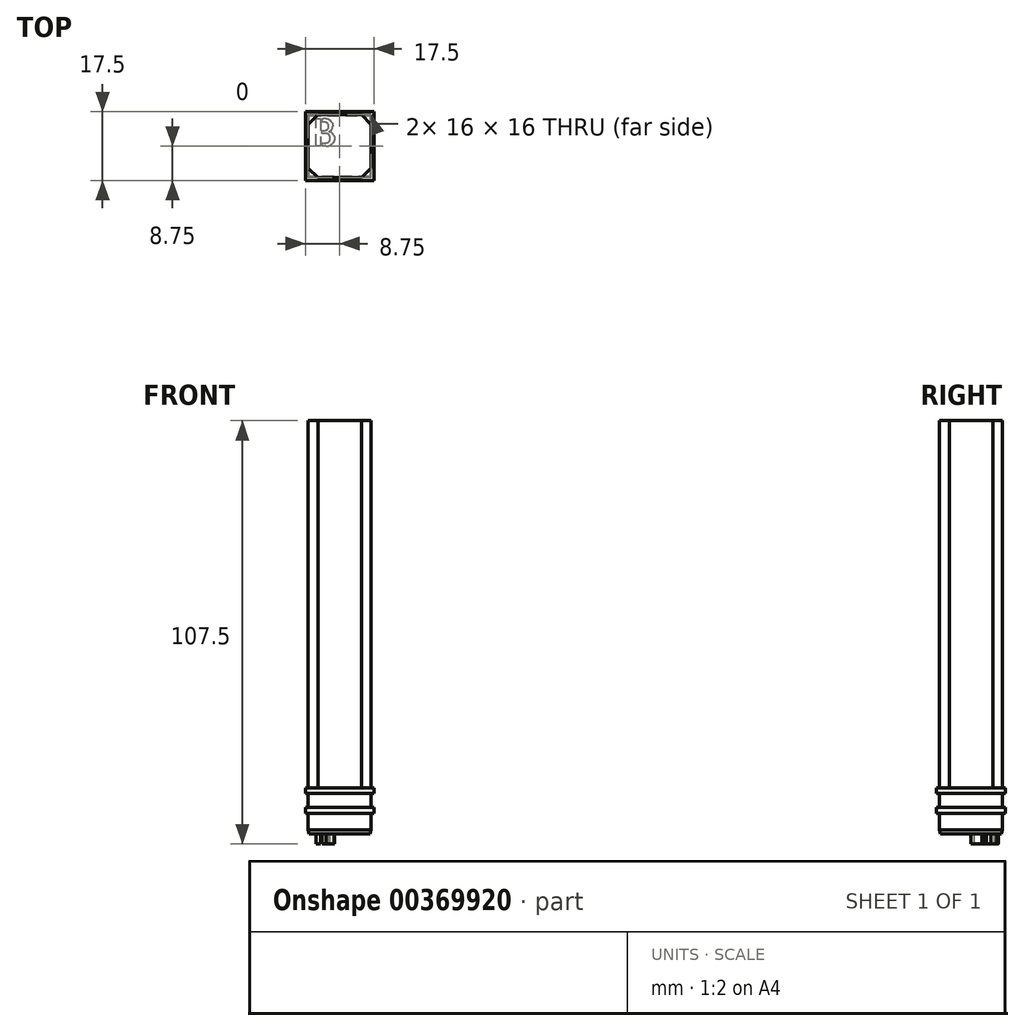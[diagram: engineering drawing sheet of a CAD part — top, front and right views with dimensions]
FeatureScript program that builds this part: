
annotation { "Feature Type Name" : "Feature", "Feature Type Description" : "" }
export const myFeature = defineFeature(function(context is Context, id is Id, definition is map)
    precondition{}
    {
        {
            var Q0;
            Q0=qCreatedBy(makeId("Top.planeOp"),FACE);
            var sketch = newSketch(context, id + "F0", { "sketchPlane" : qUnion([Q0])});
            skLineSegment(sketch, "E0.bottom", {"start": v(7.5, -7.5) * mm, "end": v(-7.5, -7.5) * mm, "construction": true});
            skLineSegment(sketch, "E0.top", {"start": v(7.5, 7.5) * mm, "end": v(-7.5, 7.5) * mm, "construction": true});
            skLineSegment(sketch, "E0.left", {"start": v(7.5, -7.5) * mm, "end": v(7.5, 7.5) * mm, "construction": true});
            skLineSegment(sketch, "E0.right", {"start": v(-7.5, -7.5) * mm, "end": v(-7.5, 7.5) * mm, "construction": true});
            skPoint(sketch, "E0.middle", {"position": v(0, 0) * mm});
            skLineSegment(sketch, "E1.0", {"start": v(8, -8) * mm, "end": v(8, 8) * mm});
            skLineSegment(sketch, "E1.1", {"start": v(8, -8) * mm, "end": v(-8, -8) * mm});
            skLineSegment(sketch, "E1.2", {"start": v(-8, -8) * mm, "end": v(-8, 8) * mm});
            skLineSegment(sketch, "E1.3", {"start": v(8, 8) * mm, "end": v(-8, 8) * mm});
            skLineSegment(sketch, "E2.0", {"start": v(7, 7) * mm, "end": v(-7, 7) * mm});
            skLineSegment(sketch, "E2.1", {"start": v(7, -7) * mm, "end": v(7, 7) * mm});
            skLineSegment(sketch, "E2.2", {"start": v(7, -7) * mm, "end": v(-7, -7) * mm});
            skLineSegment(sketch, "E2.3", {"start": v(-7, -7) * mm, "end": v(-7, 7) * mm});
            skLineSegment(sketch, "E3", {"start": v(0, 7) * mm, "end": v(0, -7) * mm, "construction": true});
            skLineSegment(sketch, "E4", {"start": v(-7, 0) * mm, "end": v(7, 0) * mm, "construction": true});
            skSolve(sketch);
        }
        {
            var Q0;
            Q0=qCreatedBy(makeId("Top.planeOp"),FACE);
            var sketch = newSketch(context, id + "F1", { "sketchPlane" : qUnion([Q0])});
            skPoint(sketch, "E5.0", {"position": v(0, 7) * mm});
            skPoint(sketch, "E6.0", {"position": v(0, 0) * mm});
            skPoint(sketch, "E7.0", {"position": v(7, 0) * mm});
            skPoint(sketch, "E8.0", {"position": v(7, 7) * mm});
            skLineSegment(sketch, "E9", {"start": v(0, 7) * mm, "end": v(0, 0) * mm, "construction": true});
            skLineSegment(sketch, "E10", {"start": v(7, 0) * mm, "end": v(0, 0) * mm, "construction": true});
            skLineSegment(sketch, "E11", {"start": v(7, 7) * mm, "end": v(7, 0) * mm, "construction": true});
            skLineSegment(sketch, "E12", {"start": v(7, 7) * mm, "end": v(0, 7) * mm, "construction": true});
            skText(sketch, "E13", { "text": "Default text", "fontName": "OpenSans-Regular.ttf"});
            skText(sketch, "E14", { "text": "Default text", "fontName": "RobotoSlab-Regular.ttf"});
            skText(sketch, "E15", { "text": "Default text", "fontName": "Tinos-Regular.ttf"});
            skText(sketch, "E16", { "text": "Default text", "fontName": "NotoSerif-Regular.ttf"});
            skText(sketch, "E17", { "text": "Default text", "fontName": "NotoSansCJKkr-Regular.otf"});
            skText(sketch, "E18", { "text": "Default text", "fontName": "NotoSansCJKjp-Regular.otf"});
            skText(sketch, "E19", { "text": "Default text", "fontName": "NotoSansCJKtc-Regular.otf"});
            skText(sketch, "E20", { "text": "Default text", "fontName": "NotoSansCJKsc-Regular.otf"});
            skText(sketch, "E21", { "text": "Default text", "fontName": "NotoSans-Regular.ttf"});
            skText(sketch, "E22", { "text": "Default text", "fontName": "DroidSansMono.ttf"});
            skText(sketch, "E23", { "text": "Default text", "fontName": "Arimo-Regular.ttf"});
            skText(sketch, "E24", { "text": "Default text", "fontName": "AllertaStencil-Regular.ttf"});
            skPoint(sketch, "E25.0", {"position": v(-7, 0) * mm});
            skPoint(sketch, "E26.0", {"position": v(-7, 7) * mm});
            skLineSegment(sketch, "E27", {"start": v(-5.99, 6.3) * mm, "end": v(-5.99, 0.6) * mm});
            skLineSegment(sketch, "E28", {"start": v(-5.99, 0.6) * mm, "end": v(-4.25, 0.6) * mm});
            skLineSegment(sketch, "E29", {"start": v(-5.99, 6.3) * mm, "end": v(-4.25, 6.3) * mm});
            skArc(sketch, "E30", {"start": v(-2.96, 3.45) * mm, "mid": v(-2.68, 5.3) * mm, "end": v(-4.25, 6.3) * mm});
            skPoint(sketch, "E30.startSnap0", {"position": v(-5.99, 3.45) * mm});
            skArc(sketch, "E31", {"start": v(-4.25, 0.6) * mm, "mid": v(-2.68, 1.6) * mm, "end": v(-2.96, 3.45) * mm});
            skLineSegment(sketch, "E32.0", {"start": v(-4.99, 6.3) * mm, "end": v(-4.99, 0.6) * mm, "construction": true});
            skLineSegment(sketch, "E33.0", {"start": v(-5.99, 1.6) * mm, "end": v(-4.25, 1.6) * mm, "construction": true});
            skLineSegment(sketch, "E34.0", {"start": v(-5.99, 5.3) * mm, "end": v(-4.25, 5.3) * mm, "construction": true});
            skLineSegment(sketch, "E35", {"start": v(-5.99, 3.45) * mm, "end": v(-4.25, 3.45) * mm, "construction": true});
            skLineSegment(sketch, "E36.0", {"start": v(-5.99, 2.95) * mm, "end": v(-4.25, 2.95) * mm, "construction": true});
            skLineSegment(sketch, "E37.0", {"start": v(-5.99, 3.95) * mm, "end": v(-4.25, 3.95) * mm, "construction": true});
            skArc(sketch, "E38", {"start": v(-4.25, 3.95) * mm, "mid": v(-3.57, 4.63) * mm, "end": v(-4.25, 5.3) * mm});
            skArc(sketch, "E39", {"start": v(-4.25, 1.6) * mm, "mid": v(-3.57, 2.27) * mm, "end": v(-4.25, 2.95) * mm});
            skLineSegment(sketch, "E40", {"start": v(-4.25, 2.95) * mm, "end": v(-4.99, 2.95) * mm});
            skLineSegment(sketch, "E41", {"start": v(-4.99, 2.95) * mm, "end": v(-4.99, 1.6) * mm});
            skLineSegment(sketch, "E42", {"start": v(-4.99, 1.6) * mm, "end": v(-4.25, 1.6) * mm});
            skLineSegment(sketch, "E43", {"start": v(-4.25, 3.95) * mm, "end": v(-4.99, 3.95) * mm});
            skLineSegment(sketch, "E44", {"start": v(-4.99, 3.95) * mm, "end": v(-4.99, 5.3) * mm});
            skLineSegment(sketch, "E45", {"start": v(-4.99, 5.3) * mm, "end": v(-4.25, 5.3) * mm});
            const initialGuessF1  = {"E13": [0.01056, 0.00091, 1, 0, 0.0074], "E14": [0.01974, -0.0134, 1, 0, 0.00915], "E15": [0.01862, -0.02922, 1, 0, 0.01054], "E16": [0.01728, -0.04803, 1, 0, 0.015], "E17": [0.0163, -0.07044, 1, 0, 0.01509], "E18": [0.01548, -0.0952, 1, 0, 0.01868], "E19": [0.01736, -0.1088, 1, 0, 0.00829], "E20": [0.0176, -0.12018, 1, 0, 0.00556], "E21": [0.0185, -0.12816, 1, 0, 0.00542], "E22": [0.01813, -0.13854, 1, 0, 0.0054], "E23": [0.01918, -0.14712, 1, 0, 0.00545], "E24": [0.0191, -0.1535, 1, 0, 0.00425]};
            skSetInitialGuess(sketch, initialGuessF1);
            skSolve(sketch);
        }
        {
            var Q0;
            Q0=makeQuery(id+"F1.imprint","IMPRINT",FACE,{"disambiguationData":[TD([[makeQuery(id+"F1.imprint","IMPRINT",EDGE,{"derivedFrom":sQuery(id+"F1.wireOp",EDGE,"E27")}),1.0]])]});
            var Q1;
            Q1=makeQuery(id+"F0.imprint","IMPRINT",FACE,{"disambiguationData":[TD([[makeQuery(id+"F0.imprint","IMPRINT",EDGE,{"derivedFrom":sQuery(id+"F0.wireOp",EDGE,"E1.0")}),1.0]])]});
            extrude(context, id + "F2", {"entities" : qUnion([Q0, Q1]), "depth" : 5 * mm, "offsetDistance" : 25 * mm});
        }
        {
            var Q0;
            Q0=makeQuery(id+"F2.opExtrude","CAP_EDGE",EDGE,{"disambiguationData":[OSD([sQuery(id+"F0.wireOp",EDGE,"E1.0")])],"isStart":true});
            var Q1;
            Q1=makeQuery(id+"F2.opExtrude","CAP_EDGE",EDGE,{"disambiguationData":[OSD([sQuery(id+"F0.wireOp",EDGE,"E1.1")])],"isStart":true});
            var Q2;
            Q2=makeQuery(id+"F2.opExtrude","CAP_EDGE",EDGE,{"disambiguationData":[OSD([sQuery(id+"F0.wireOp",EDGE,"E1.2")])],"isStart":true});
            var Q3;
            Q3=makeQuery(id+"F2.opExtrude","CAP_EDGE",EDGE,{"disambiguationData":[OSD([sQuery(id+"F0.wireOp",EDGE,"E1.3")])],"isStart":true});
            var Q4;
            Q4=makeQuery(id+"F2.opExtrude","CAP_EDGE",EDGE,{"disambiguationData":[OSD([sQuery(id+"F0.wireOp",EDGE,"E2.1")])],"isStart":true});
            var Q5;
            Q5=makeQuery(id+"F2.opExtrude","CAP_EDGE",EDGE,{"disambiguationData":[OSD([sQuery(id+"F0.wireOp",EDGE,"E2.0")])],"isStart":true});
            var Q6;
            Q6=makeQuery(id+"F2.opExtrude","CAP_EDGE",EDGE,{"disambiguationData":[OSD([sQuery(id+"F0.wireOp",EDGE,"E2.3")])],"isStart":true});
            var Q7;
            Q7=makeQuery(id+"F2.opExtrude","CAP_EDGE",EDGE,{"disambiguationData":[OSD([sQuery(id+"F0.wireOp",EDGE,"E2.2")])],"isStart":true});
            chamfer(context, id + "F3", {"entities" : qUnion([Q0, Q1, Q2, Q3, Q4, Q5, Q6, Q7]), "chamferType" : ChamferType.TWO_OFFSETS, "width1" : 1 * mm, "oppositeDirection" : false, "width2" : .25 * mm, "tangentPropagation" : true});
        }
        {
            var Q0;
            Q0=makeQuery(id+"F2.opExtrude","CAP_EDGE",EDGE,{"disambiguationData":[OSD([sQuery(id+"F1.wireOp",EDGE,"E27")])],"isStart":true});
            var Q1;
            Q1=makeQuery(id+"F2.opExtrude","CAP_EDGE",EDGE,{"disambiguationData":[OSD([sQuery(id+"F1.wireOp",EDGE,"E28")])],"isStart":true});
            var Q2;
            Q2=makeQuery(id+"F2.opExtrude","CAP_EDGE",EDGE,{"disambiguationData":[OSD([sQuery(id+"F1.wireOp",EDGE,"E31")])],"isStart":true});
            var Q3;
            Q3=makeQuery(id+"F2.opExtrude","CAP_EDGE",EDGE,{"disambiguationData":[OSD([sQuery(id+"F1.wireOp",EDGE,"E30")])],"isStart":true});
            var Q4;
            Q4=makeQuery(id+"F2.opExtrude","CAP_EDGE",EDGE,{"disambiguationData":[OSD([sQuery(id+"F1.wireOp",EDGE,"E29")])],"isStart":true});
            var Q5;
            Q5=makeQuery(id+"F2.opExtrude","CAP_EDGE",EDGE,{"disambiguationData":[OSD([sQuery(id+"F1.wireOp",EDGE,"E40")])],"isStart":true});
            var Q6;
            Q6=makeQuery(id+"F2.opExtrude","CAP_EDGE",EDGE,{"disambiguationData":[OSD([sQuery(id+"F1.wireOp",EDGE,"E41")])],"isStart":true});
            var Q7;
            Q7=makeQuery(id+"F2.opExtrude","CAP_EDGE",EDGE,{"disambiguationData":[OSD([sQuery(id+"F1.wireOp",EDGE,"E44")])],"isStart":true});
            var Q8;
            Q8=makeQuery(id+"F2.opExtrude","CAP_EDGE",EDGE,{"disambiguationData":[OSD([sQuery(id+"F1.wireOp",EDGE,"E45")])],"isStart":true});
            chamfer(context, id + "F4", {"entities" : qUnion([Q0, Q1, Q2, Q3, Q4, Q5, Q6, Q7, Q8]), "chamferType" : ChamferType.TWO_OFFSETS, "width1" : 1 * mm, "oppositeDirection" : false, "width2" : .25 * mm, "tangentPropagation" : true});
        }
        {
            var Q0;
            Q0=makeQuery(id+"F2.opExtrude","CAP_FACE",FACE,{"disambiguationData":[OSD([sQuery(id+"F0.wireOp",EDGE,"E1.0"),sQuery(id+"F0.wireOp",EDGE,"E1.1"),sQuery(id+"F0.wireOp",EDGE,"E1.2"),sQuery(id+"F0.wireOp",EDGE,"E1.3"),sQuery(id+"F0.wireOp",EDGE,"E2.0"),sQuery(id+"F0.wireOp",EDGE,"E2.1"),sQuery(id+"F0.wireOp",EDGE,"E2.2"),sQuery(id+"F0.wireOp",EDGE,"E2.3")])],"isStart":false});
            var sketch = newSketch(context, id + "F5", { "sketchPlane" : qUnion([Q0])});
            skPoint(sketch, "E46.0", {"position": v(-8, 8) * mm});
            skPoint(sketch, "E47.0", {"position": v(7, 7) * mm});
            skPoint(sketch, "E48.0", {"position": v(-8, -8) * mm});
            skPoint(sketch, "E49.0", {"position": v(8, -8) * mm});
            skLineSegment(sketch, "E50.bottom", {"start": v(-8, 8) * mm, "end": v(8, 8) * mm});
            skLineSegment(sketch, "E50.top", {"start": v(-8, -8) * mm, "end": v(8, -8) * mm});
            skLineSegment(sketch, "E50.left", {"start": v(-8, 8) * mm, "end": v(-8, -8) * mm});
            skLineSegment(sketch, "E50.right", {"start": v(8, 8) * mm, "end": v(8, -8) * mm});
            skSolve(sketch);
        }
        {
            var Q0;
            Q0 = qSketchRegion(id + "F5", true);
            extrude(context, id + "F6", {"entities" : qUnion([Q0]), "depth" : 25 * mm, "offsetDistance" : 25 * mm, "hasSecondDirection" : true, "secondDirectionOppositeDirection" : true, "secondDirectionDepth" : 4 * mm});
        }
        {
            var Q0;
            Q0=makeQuery(id+"F6.opExtrude","CAP_FACE",FACE,{"disambiguationData":[OSD([sQuery(id+"F5.wireOp",EDGE,"E50.bottom"),sQuery(id+"F5.wireOp",EDGE,"E50.top"),sQuery(id+"F5.wireOp",EDGE,"E50.left"),sQuery(id+"F5.wireOp",EDGE,"E50.right")])],"isStart":false});
            extrude(context, id + "F7", {"entities" : qUnion([Q0]), "operationType" : NewBodyOperationType.ADD, "depth" : 25 * mm, "offsetDistance" : 25 * mm});
        }
        {
            var Q0;
            Q0=makeQuery(id+"F6.boolean.opBoolean","SPLIT",FACE,{"disambiguationData":[TD([makeQuery(id+"F3.opChamfer","BLEND_FACE",FACE,{"disambiguationData":[OSD([sQuery(id+"F0.wireOp",EDGE,"E2.0")])]})])],"derivedFrom":makeQuery(id+"F6.opExtrude","CAP_FACE",FACE,{"disambiguationData":[OSD([sQuery(id+"F5.wireOp",EDGE,"E50.bottom"),sQuery(id+"F5.wireOp",EDGE,"E50.top"),sQuery(id+"F5.wireOp",EDGE,"E50.left"),sQuery(id+"F5.wireOp",EDGE,"E50.right")])],"isStart":true})});
            cPlane(context, id + "F8", {"entities" : qUnion([Q0]), "cplaneType" : CPlaneType.OFFSET, "offset" : 5 * mm, "oppositeDirection" : true, "width" : 150 * mm, "height" : 150 * mm});
        }
        {
            var Q0;
            Q0=qCreatedBy(id+"F8.planeOp",FACE);
            cPlane(context, id + "F9", {"entities" : qUnion([Q0]), "cplaneType" : CPlaneType.OFFSET, "offset" : 5 * mm, "oppositeDirection" : true, "width" : 150 * mm, "height" : 150 * mm});
        }
        {
            var Q0;
            Q0=qCreatedBy(id+"F8.planeOp",FACE);
            var sketch = newSketch(context, id + "F10", { "sketchPlane" : qUnion([Q0])});
            skLineSegment(sketch, "E51.0.1", {"start": v(-8, -8) * mm, "end": v(-8, 8) * mm});
            skLineSegment(sketch, "E51.0.3", {"start": v(-8, 8) * mm, "end": v(-8, -8) * mm});
            skLineSegment(sketch, "E52.0.1", {"start": v(8, -8) * mm, "end": v(-8, -8) * mm});
            skLineSegment(sketch, "E52.0.3", {"start": v(-8, -8) * mm, "end": v(8, -8) * mm});
            skLineSegment(sketch, "E53.0.1", {"start": v(8, 8) * mm, "end": v(8, -8) * mm});
            skLineSegment(sketch, "E53.0.3", {"start": v(8, -8) * mm, "end": v(8, 8) * mm});
            skLineSegment(sketch, "E54.0.1", {"start": v(-8, 8) * mm, "end": v(8, 8) * mm});
            skLineSegment(sketch, "E54.0.3", {"start": v(8, 8) * mm, "end": v(-8, 8) * mm});
            skSolve(sketch);
        }
        {
            var Q0;
            Q0=qCreatedBy(id+"F9.planeOp",FACE);
            var sketch = newSketch(context, id + "F11", { "sketchPlane" : qUnion([Q0])});
            skLineSegment(sketch, "E55.0.1", {"start": v(-8, 8) * mm, "end": v(8, 8) * mm});
            skLineSegment(sketch, "E55.0.3", {"start": v(8, 8) * mm, "end": v(-8, 8) * mm});
            skLineSegment(sketch, "E56.0.1", {"start": v(8, 8) * mm, "end": v(8, -8) * mm});
            skLineSegment(sketch, "E56.0.3", {"start": v(8, -8) * mm, "end": v(8, 8) * mm});
            skLineSegment(sketch, "E57.0.1", {"start": v(-8, -8) * mm, "end": v(-8, 8) * mm});
            skLineSegment(sketch, "E57.0.3", {"start": v(-8, 8) * mm, "end": v(-8, -8) * mm});
            skLineSegment(sketch, "E58.0.1", {"start": v(8, -8) * mm, "end": v(-8, -8) * mm});
            skLineSegment(sketch, "E58.0.3", {"start": v(-8, -8) * mm, "end": v(8, -8) * mm});
            skSolve(sketch);
        }
        {
            var Q0;
            Q0=makeQuery(id+"F6.opExtrude","SWEPT_FACE",FACE,{"disambiguationData":[OSD([sQuery(id+"F5.wireOp",EDGE,"E50.bottom")])]});
            cPlane(context, id + "F12", {"entities" : qUnion([Q0]), "cplaneType" : CPlaneType.OFFSET, "offset" : 7.5 * mm, "oppositeDirection" : true, "width" : 150 * mm, "height" : 150 * mm});
        }
        {
            var Q0;
            Q0=qCreatedBy(id+"F12.planeOp",FACE);
            var sketch = newSketch(context, id + "F13", { "sketchPlane" : qUnion([Q0])});
            skPoint(sketch, "E59.0", {"position": v(8, 6) * mm});
            skPoint(sketch, "E60.0", {"position": v(8, 11) * mm});
            skLineSegment(sketch, "E61.bottom", {"start": v(8.75, 10.25) * mm, "end": v(7.25, 10.25) * mm});
            skLineSegment(sketch, "E61.top", {"start": v(8.75, 11.75) * mm, "end": v(7.25, 11.75) * mm});
            skLineSegment(sketch, "E61.left", {"start": v(8.75, 10.25) * mm, "end": v(8.75, 11.75) * mm});
            skLineSegment(sketch, "E61.right", {"start": v(7.25, 10.25) * mm, "end": v(7.25, 11.75) * mm});
            skLineSegment(sketch, "E62.bottom", {"start": v(8.75, 5.25) * mm, "end": v(7.25, 5.25) * mm});
            skLineSegment(sketch, "E62.top", {"start": v(8.75, 6.75) * mm, "end": v(7.25, 6.75) * mm});
            skLineSegment(sketch, "E62.left", {"start": v(8.75, 5.25) * mm, "end": v(8.75, 6.75) * mm});
            skLineSegment(sketch, "E62.right", {"start": v(7.25, 5.25) * mm, "end": v(7.25, 6.75) * mm});
            skSolve(sketch);
        }
        {
            var Q0;
            Q0=makeQuery(id+"F13.imprint","IMPRINT",FACE,{"disambiguationData":[TD([[makeQuery(id+"F13.imprint","IMPRINT",EDGE,{"derivedFrom":sQuery(id+"F13.wireOp",EDGE,"E61.bottom")}),-1.0]])]});
            var Q1;
            Q1=makeQuery(id+"F13.imprint","IMPRINT",FACE,{"disambiguationData":[TD([[makeQuery(id+"F13.imprint","IMPRINT",EDGE,{"derivedFrom":sQuery(id+"F13.wireOp",EDGE,"E62.bottom")}),-1.0]])]});
            var Q2;
            Q2=sQuery(id+"F10.wireOp",EDGE,"E51.0.3");
            var Q3;
            Q3=sQuery(id+"F10.wireOp",EDGE,"E52.0.3");
            var Q4;
            Q4=sQuery(id+"F10.wireOp",EDGE,"E54.0.1");
            var Q5;
            Q5=sQuery(id+"F10.wireOp",EDGE,"E53.0.3");
            sweep(context, id + "F14", {"operationType" : NewBodyOperationType.REMOVE, "profiles" : qUnion([Q0, Q1]), "path" : qUnion([Q2, Q3, Q4, Q5])});
        }
        {
            var Q0;
            Q0=makeQuery(id+"F2.opExtrude","CAP_FACE",FACE,{"disambiguationData":[OSD([sQuery(id+"F1.wireOp",EDGE,"E27"),sQuery(id+"F1.wireOp",EDGE,"E28"),sQuery(id+"F1.wireOp",EDGE,"E29"),sQuery(id+"F1.wireOp",EDGE,"E30"),sQuery(id+"F1.wireOp",EDGE,"E31"),sQuery(id+"F1.wireOp",EDGE,"E38"),sQuery(id+"F1.wireOp",EDGE,"E39"),sQuery(id+"F1.wireOp",EDGE,"E40"),sQuery(id+"F1.wireOp",EDGE,"E41"),sQuery(id+"F1.wireOp",EDGE,"E42"),sQuery(id+"F1.wireOp",EDGE,"E43"),sQuery(id+"F1.wireOp",EDGE,"E44"),sQuery(id+"F1.wireOp",EDGE,"E45")])],"isStart":true});
            var sketch = newSketch(context, id + "F15", { "sketchPlane" : qUnion([Q0])});
            skPoint(sketch, "E63.0", {"position": v(-5.99, -0.6) * mm});
            skPoint(sketch, "E64.0", {"position": v(-4.25, -0.6) * mm});
            skPoint(sketch, "E65.0", {"position": v(-4.99, -1.6) * mm});
            skPoint(sketch, "E66.0", {"position": v(-4.25, -1.6) * mm});
            skPoint(sketch, "E67.0", {"position": v(-4.25, -3.95) * mm});
            skLineSegment(sketch, "E68.0", {"start": v(-4.25, -3.95) * mm, "end": v(-4.99, -3.95) * mm, "construction": true});
            skPoint(sketch, "E69.0", {"position": v(-5.99, -6.3) * mm});
            skPoint(sketch, "E70.0", {"position": v(-4.25, -6.3) * mm});
            skLineSegment(sketch, "E71.0", {"start": v(-4.99, -5.3) * mm, "end": v(-4.25, -5.3) * mm, "construction": true});
            skLineSegment(sketch, "E72.0", {"start": v(-4.99, -3.95) * mm, "end": v(-4.99, -5.3) * mm});
            skLineSegment(sketch, "E73.0", {"start": v(-4.99, -2.95) * mm, "end": v(-4.25, -2.95) * mm});
            skLineSegment(sketch, "E74.0", {"start": v(-4.99, -1.6) * mm, "end": v(-4.99, -2.95) * mm});
            skLineSegment(sketch, "E75.0", {"start": v(-4.25, -1.6) * mm, "end": v(-4.99, -1.6) * mm});
            skLineSegment(sketch, "E76.0", {"start": v(-5.99, -6.3) * mm, "end": v(-5.99, -0.6) * mm});
            skLineSegment(sketch, "E77.0", {"start": v(-5.99, -0.6) * mm, "end": v(-4.25, -0.6) * mm});
            skPoint(sketch, "E78.0", {"position": v(-2.96, -3.45) * mm});
            skLineSegment(sketch, "E79.0", {"start": v(-4.25, -6.3) * mm, "end": v(-5.99, -6.3) * mm, "construction": true});
            skArc(sketch, "E80.0", {"start": v(-4.25, -2.95) * mm, "mid": v(-3.57, -2.27) * mm, "end": v(-4.25, -1.6) * mm});
            skArc(sketch, "E81.0", {"start": v(-4.25, -0.6) * mm, "mid": v(-2.68, -1.6) * mm, "end": v(-2.96, -3.45) * mm, "construction": true});
            skLineSegment(sketch, "E82", {"start": v(-4.99, -3.95) * mm, "end": v(-4.49, -3.95) * mm});
            skLineSegment(sketch, "E83", {"start": v(-4.99, -5.3) * mm, "end": v(-4.49, -5.3) * mm});
            skLineSegment(sketch, "E84", {"start": v(-4.49, -5.3) * mm, "end": v(-4.49, -6.3) * mm, "construction": true});
            skLineSegment(sketch, "E85", {"start": v(-5.99, -6.3) * mm, "end": v(-4.49, -6.3) * mm});
            skArc(sketch, "E86", {"start": v(-4.49, -5.3) * mm, "mid": v(-3.81, -4.63) * mm, "end": v(-4.49, -3.95) * mm});
            skArc(sketch, "E87", {"start": v(-4.49, -6.3) * mm, "mid": v(-2.87, -5.33) * mm, "end": v(-2.96, -3.45) * mm, "construction": true});
            skArc(sketch, "E88", {"start": v(-4.25, -0.6) * mm, "mid": v(-2.64, -1.72) * mm, "end": v(-3.14, -3.62) * mm});
            skArc(sketch, "E89", {"start": v(-4.49, -6.3) * mm, "mid": v(-2.99, -5.38) * mm, "end": v(-3.14, -3.62) * mm});
            skSolve(sketch);
        }
        {
            var Q0;
            Q0 = qSketchRegion(id + "F15", true);
            extrude(context, id + "F16", {"entities" : qUnion([Q0]), "operationType" : NewBodyOperationType.ADD, "oppositeDirection" : true, "depth" : 25 * mm, "offsetDistance" : 25 * mm});
        }
        {
            var Q0;
            Q0=makeQuery(id+"F16.opExtrude","CAP_EDGE",EDGE,{"disambiguationData":[OSD([sQuery(id+"F15.wireOp",EDGE,"E85")])],"isStart":true});
            var Q1;
            Q1=makeQuery(id+"F16.opExtrude","CAP_EDGE",EDGE,{"disambiguationData":[OSD([sQuery(id+"F15.wireOp",EDGE,"E76.0")])],"isStart":true});
            var Q2;
            Q2=makeQuery(id+"F16.opExtrude","CAP_EDGE",EDGE,{"disambiguationData":[OSD([sQuery(id+"F15.wireOp",EDGE,"E77.0")])],"isStart":true});
            var Q3;
            Q3=makeQuery(id+"F16.opExtrude","CAP_EDGE",EDGE,{"disambiguationData":[OSD([sQuery(id+"F15.wireOp",EDGE,"E89")])],"isStart":true});
            var Q4;
            Q4=makeQuery(id+"F16.opExtrude","CAP_EDGE",EDGE,{"disambiguationData":[OSD([sQuery(id+"F15.wireOp",EDGE,"E88")])],"isStart":true});
            var Q5;
            Q5=makeQuery(id+"F16.opExtrude","CAP_EDGE",EDGE,{"disambiguationData":[OSD([sQuery(id+"F15.wireOp",EDGE,"E74.0")])],"isStart":true});
            var Q6;
            Q6=makeQuery(id+"F16.opExtrude","CAP_EDGE",EDGE,{"disambiguationData":[OSD([sQuery(id+"F15.wireOp",EDGE,"E75.0")])],"isStart":true});
            var Q7;
            Q7=makeQuery(id+"F16.opExtrude","CAP_EDGE",EDGE,{"disambiguationData":[OSD([sQuery(id+"F15.wireOp",EDGE,"E80.0")])],"isStart":true});
            var Q8;
            Q8=makeQuery(id+"F16.opExtrude","CAP_EDGE",EDGE,{"disambiguationData":[OSD([sQuery(id+"F15.wireOp",EDGE,"E73.0")])],"isStart":true});
            var Q9;
            Q9=makeQuery(id+"F16.opExtrude","CAP_EDGE",EDGE,{"disambiguationData":[OSD([sQuery(id+"F15.wireOp",EDGE,"E72.0")])],"isStart":true});
            var Q10;
            Q10=makeQuery(id+"F16.opExtrude","CAP_EDGE",EDGE,{"disambiguationData":[OSD([sQuery(id+"F15.wireOp",EDGE,"E82")])],"isStart":true});
            var Q11;
            Q11=makeQuery(id+"F16.opExtrude","CAP_EDGE",EDGE,{"disambiguationData":[OSD([sQuery(id+"F15.wireOp",EDGE,"E83")])],"isStart":true});
            var Q12;
            Q12=makeQuery(id+"F16.opExtrude","CAP_EDGE",EDGE,{"disambiguationData":[OSD([sQuery(id+"F15.wireOp",EDGE,"E86")])],"isStart":true});
            chamfer(context, id + "F17", {"entities" : qUnion([Q0, Q1, Q2, Q3, Q4, Q5, Q6, Q7, Q8, Q9, Q10, Q11, Q12]), "chamferType" : ChamferType.TWO_OFFSETS, "width1" : .25 * mm, "oppositeDirection" : false, "width2" : 1 * mm, "tangentPropagation" : true});
        }
        {
            var Q0;
            Q0=qCreatedBy(makeId("Top.planeOp"),FACE);
            var sketch = newSketch(context, id + "F18", { "sketchPlane" : qUnion([Q0])});
            skLineSegment(sketch, "E90.0.0", {"start": v(8, 8) * mm, "end": v(8, -8) * mm});
            skLineSegment(sketch, "E90.0.1", {"start": v(8, -8) * mm, "end": v(-8, -8) * mm});
            skLineSegment(sketch, "E90.0.2", {"start": v(-8, -8) * mm, "end": v(-8, 8) * mm});
            skLineSegment(sketch, "E90.0.3", {"start": v(-8, 8) * mm, "end": v(8, 8) * mm});
            skPoint(sketch, "E91.0", {"position": v(-7.5, 7.5) * mm});
            skPoint(sketch, "E92.0", {"position": v(-7.5, -7.5) * mm});
            skPoint(sketch, "E93.0", {"position": v(7.5, -7.5) * mm});
            skPoint(sketch, "E94.0", {"position": v(7.5, 7.5) * mm});
            skText(sketch, "E95", { "text": "B", "fontName": "AllertaStencil-Regular.ttf"});
            const initialGuessF18  = {"E95": [-0.00697, 2e-05, 1, 0, 0.00697]};
            skSetInitialGuess(sketch, initialGuessF18);
            skSolve(sketch);
        }
        {
            var Q0;
            Q0=makeQuery(id+"F18.imprint","IMPRINT",FACE,{"disambiguationData":[TD([[makeQuery(id+"F18.imprint","IMPRINT",EDGE,{"derivedFrom":sQuery(id+"F18.wireOp",EDGE,"E95.sketch_text.stroke-0")}),-1.0]])]});
            var Q1;
            Q1=makeQuery(id+"F18.imprint","IMPRINT",FACE,{"disambiguationData":[TD([[makeQuery(id+"F18.imprint","IMPRINT",EDGE,{"derivedFrom":sQuery(id+"F18.wireOp",EDGE,"E95.sketch_text.stroke-39")}),-1.0]])]});
            extrude(context, id + "F19", {"entities" : qUnion([Q0, Q1]), "oppositeDirection" : true, "depth" : 2.5 * mm, "offsetDistance" : 25 * mm});
        }
        {
            var Q0;
            Q0=makeQuery(id+"F0.imprint","IMPRINT",FACE,{"disambiguationData":[TD([[makeQuery(id+"F0.imprint","IMPRINT",EDGE,{"derivedFrom":sQuery(id+"F0.wireOp",EDGE,"E1.0")}),1.0]])]});
            var Q1;
            Q1=makeQuery(id+"F0.imprint","IMPRINT",FACE,{"disambiguationData":[TD([[makeQuery(id+"F0.imprint","IMPRINT",EDGE,{"derivedFrom":sQuery(id+"F0.wireOp",EDGE,"E2.0")}),1.0]])]});
            extrude(context, id + "F20", {"entities" : qUnion([Q0, Q1]), "depth" : 5 * mm, "offsetDistance" : 25 * mm});
        }
        {
            var Q0;
            Q0=makeQuery(id+"F20.opExtrude","CAP_EDGE",EDGE,{"disambiguationData":[OSD([sQuery(id+"F0.wireOp",EDGE,"E1.3")])],"isStart":true});
            var Q1;
            Q1=makeQuery(id+"F20.opExtrude","CAP_EDGE",EDGE,{"disambiguationData":[OSD([sQuery(id+"F0.wireOp",EDGE,"E1.2")])],"isStart":true});
            var Q2;
            Q2=makeQuery(id+"F20.opExtrude","CAP_EDGE",EDGE,{"disambiguationData":[OSD([sQuery(id+"F0.wireOp",EDGE,"E1.1")])],"isStart":true});
            var Q3;
            Q3=makeQuery(id+"F20.opExtrude","CAP_EDGE",EDGE,{"disambiguationData":[OSD([sQuery(id+"F0.wireOp",EDGE,"E1.0")])],"isStart":true});
            chamfer(context, id + "F21", {"entities" : qUnion([Q0, Q1, Q2, Q3]), "chamferType" : ChamferType.TWO_OFFSETS, "width1" : 2 * mm, "oppositeDirection" : false, "width2" : .5 * mm, "tangentPropagation" : true});
        }
        {
            var Q0;
            Q0=makeQuery(id+"F20.opExtrude","CAP_FACE",FACE,{"disambiguationData":[OSD([sQuery(id+"F0.wireOp",EDGE,"E1.0"),sQuery(id+"F0.wireOp",EDGE,"E1.1"),sQuery(id+"F0.wireOp",EDGE,"E1.2"),sQuery(id+"F0.wireOp",EDGE,"E1.3")])],"isStart":false});
            extrude(context, id + "F22", {"entities" : qUnion([Q0]), "operationType" : NewBodyOperationType.ADD, "depth" : 100 * mm, "offsetDistance" : 25 * mm});
        }
        {
            var Q0;
            Q0=makeQuery(id+"F13.imprint","IMPRINT",FACE,{"disambiguationData":[TD([[makeQuery(id+"F13.imprint","IMPRINT",EDGE,{"derivedFrom":sQuery(id+"F13.wireOp",EDGE,"E62.bottom")}),-1.0]])]});
            var Q1;
            Q1=makeQuery(id+"F13.imprint","IMPRINT",FACE,{"disambiguationData":[TD([[makeQuery(id+"F13.imprint","IMPRINT",EDGE,{"derivedFrom":sQuery(id+"F13.wireOp",EDGE,"E61.bottom")}),-1.0]])]});
            var Q2;
            Q2=sQuery(id+"F11.wireOp",EDGE,"E57.0.3");
            var Q3;
            Q3=sQuery(id+"F11.wireOp",EDGE,"E58.0.3");
            var Q4;
            Q4=sQuery(id+"F11.wireOp",EDGE,"E56.0.1");
            var Q5;
            Q5=sQuery(id+"F11.wireOp",EDGE,"E55.0.1");
            sweep(context, id + "F23", {"operationType" : NewBodyOperationType.ADD, "profiles" : qUnion([Q0, Q1]), "path" : qUnion([Q2, Q3, Q4, Q5])});
        }
        {
            var Q0;
            {var subQ0=sQuery(id+"F0.wireOp",EDGE,"E1.3");var subQ1=sQuery(id+"F0.wireOp",EDGE,"E1.2");Q0=makeQuery(id+"F23.boolean.opBoolean","SPLIT",EDGE,{"disambiguationData":[TD([makeQuery(id+"F23.opSweep","SWEPT_FACE",FACE,{"disambiguationData":[OSD([sQuery(id+"F11.wireOp",EDGE,"E58.0.3"),sQuery(id+"F13.wireOp",EDGE,"E61.top")])]})])],"derivedFrom":makeQuery(id+"F22.boolean.opBoolean","MERGE",EDGE,{"derivedFrom":[makeQuery(id+"F20.opExtrude","SWEPT_EDGE",EDGE,{"disambiguationData":[OSD([subQ1,subQ0])]}),makeQuery(id+"F22.opExtrude","SWEPT_EDGE",EDGE,{"disambiguationData":[OSD([subQ1,subQ0])]})]})});}
            var Q1;
            {var subQ0=sQuery(id+"F0.wireOp",EDGE,"E1.2");var subQ1=sQuery(id+"F0.wireOp",EDGE,"E1.1");Q1=makeQuery(id+"F23.boolean.opBoolean","SPLIT",EDGE,{"disambiguationData":[TD([makeQuery(id+"F23.opSweep","SWEPT_FACE",FACE,{"disambiguationData":[OSD([sQuery(id+"F11.wireOp",EDGE,"E58.0.3"),sQuery(id+"F13.wireOp",EDGE,"E61.top")])]})])],"derivedFrom":makeQuery(id+"F22.boolean.opBoolean","MERGE",EDGE,{"derivedFrom":[makeQuery(id+"F20.opExtrude","SWEPT_EDGE",EDGE,{"disambiguationData":[OSD([subQ1,subQ0])]}),makeQuery(id+"F22.opExtrude","SWEPT_EDGE",EDGE,{"disambiguationData":[OSD([subQ1,subQ0])]})]})});}
            var Q2;
            {var subQ0=sQuery(id+"F0.wireOp",EDGE,"E1.0");var subQ1=sQuery(id+"F0.wireOp",EDGE,"E1.1");Q2=makeQuery(id+"F23.boolean.opBoolean","SPLIT",EDGE,{"disambiguationData":[TD([makeQuery(id+"F23.opSweep","SWEPT_FACE",FACE,{"disambiguationData":[OSD([sQuery(id+"F11.wireOp",EDGE,"E58.0.3"),sQuery(id+"F13.wireOp",EDGE,"E61.top")])]})])],"derivedFrom":makeQuery(id+"F22.boolean.opBoolean","MERGE",EDGE,{"derivedFrom":[makeQuery(id+"F20.opExtrude","SWEPT_EDGE",EDGE,{"disambiguationData":[OSD([subQ0,subQ1])]}),makeQuery(id+"F22.opExtrude","SWEPT_EDGE",EDGE,{"disambiguationData":[OSD([subQ0,subQ1])]})]})});}
            var Q3;
            {var subQ0=sQuery(id+"F0.wireOp",EDGE,"E1.0");var subQ1=sQuery(id+"F0.wireOp",EDGE,"E1.3");Q3=makeQuery(id+"F23.boolean.opBoolean","SPLIT",EDGE,{"disambiguationData":[TD([makeQuery(id+"F23.opSweep","SWEPT_FACE",FACE,{"disambiguationData":[OSD([sQuery(id+"F11.wireOp",EDGE,"E58.0.3"),sQuery(id+"F13.wireOp",EDGE,"E61.top")])]})])],"derivedFrom":makeQuery(id+"F22.boolean.opBoolean","MERGE",EDGE,{"derivedFrom":[makeQuery(id+"F20.opExtrude","SWEPT_EDGE",EDGE,{"disambiguationData":[OSD([subQ0,subQ1])]}),makeQuery(id+"F22.opExtrude","SWEPT_EDGE",EDGE,{"disambiguationData":[OSD([subQ0,subQ1])]})]})});}
            chamfer(context, id + "F24", {"entities" : qUnion([Q0, Q1, Q2, Q3]), "width" : 2.5 * mm, "tangentPropagation" : true});
        }
    });
